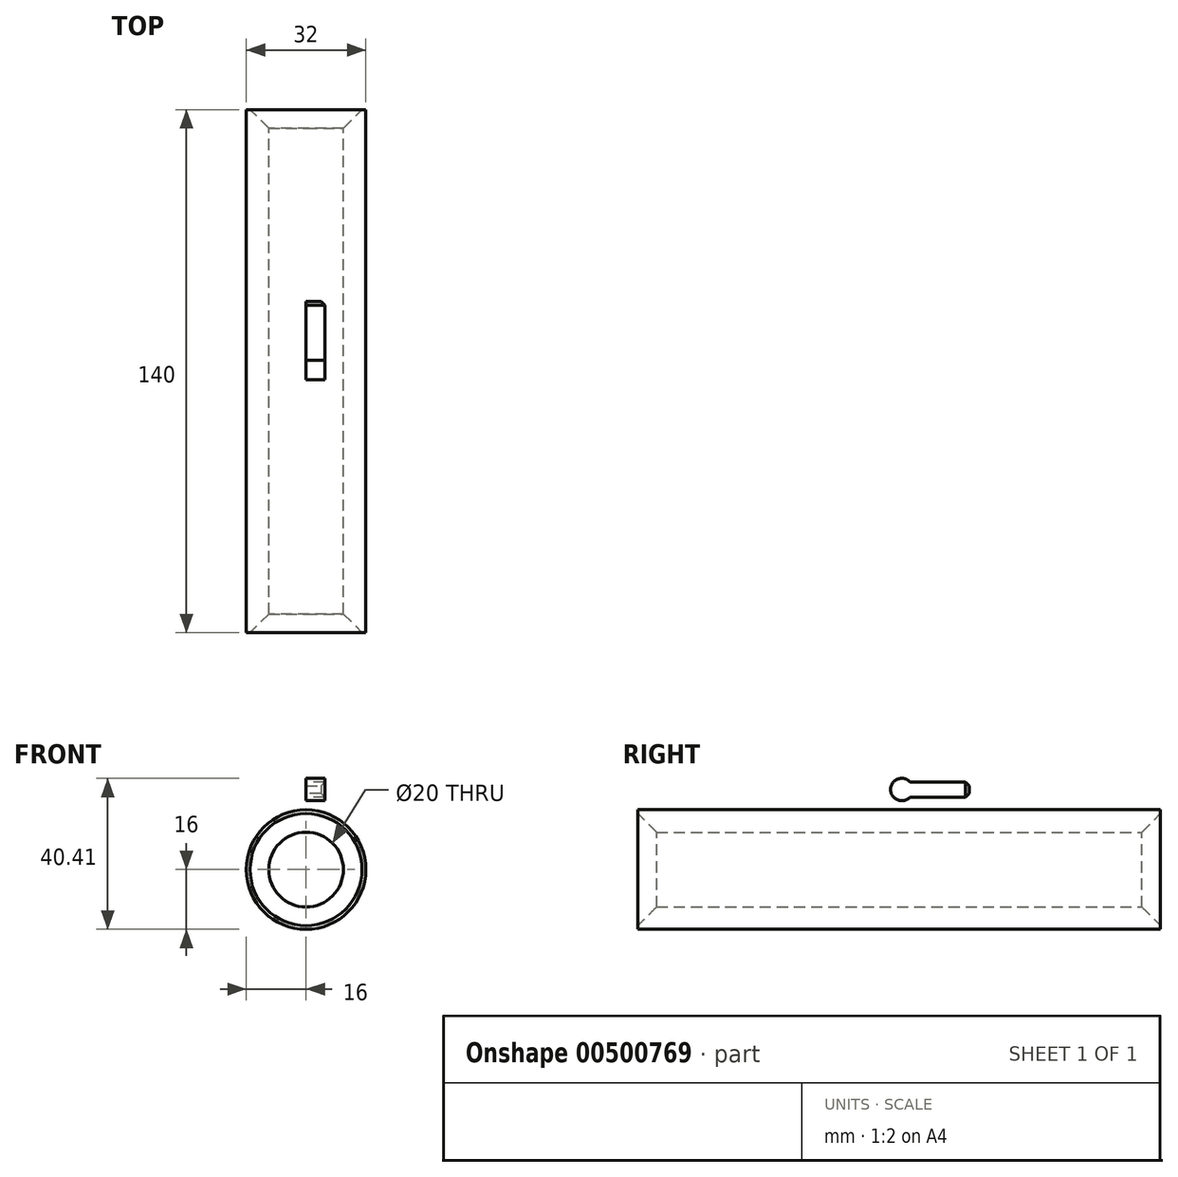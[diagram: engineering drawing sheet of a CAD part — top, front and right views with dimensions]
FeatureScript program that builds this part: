
annotation { "Feature Type Name" : "Feature", "Feature Type Description" : "" }
export const myFeature = defineFeature(function(context is Context, id is Id, definition is map)
    precondition{}
    {
        {
            var Q0;
            Q0=qCreatedBy(makeId("Front.planeOp"),FACE);
            var sketch = newSketch(context, id + "F0", { "sketchPlane" : qUnion([Q0])});
            skCircle(sketch, "E0", {"center": v(0, 0) * mm, "radius": 10 * mm});
            skCircle(sketch, "E1", {"center": v(0, 0) * mm, "radius": 16 * mm});
            skSolve(sketch);
        }
        {
            var Q0;
            Q0=makeQuery(id+"F0.imprint","IMPRINT",FACE,{"disambiguationData":[TD([[makeQuery(id+"F0.imprint","IMPRINT",EDGE,{"derivedFrom":sQuery(id+"F0.wireOp",EDGE,"E0")}),-1.0]])]});
            extrude(context, id + "F1", {"entities" : qUnion([Q0]), "depth" : 140 * mm});
        }
        {
            var Q0;
            Q0=makeQuery(id+"F1.opExtrude","CAP_EDGE",EDGE,{"disambiguationData":[OSD([sQuery(id+"F0.wireOp",EDGE,"E0")])],"isStart":false});
            var Q1;
            Q1=makeQuery(id+"F1.opExtrude","CAP_EDGE",EDGE,{"disambiguationData":[OSD([sQuery(id+"F0.wireOp",EDGE,"E0")])],"isStart":true});
            chamfer(context, id + "F2", {"entities" : qUnion([Q0, Q1]), "width" : 5 * mm, "tangentPropagation" : true});
        }
        {
            var Q0;
            Q0=qCreatedBy(makeId("Right.planeOp"),FACE);
            var sketch = newSketch(context, id + "F3", { "sketchPlane" : qUnion([Q0])});
            skLineSegment(sketch, "E2.bottom", {"start": v(-69.3, 23.4) * mm, "end": v(-51.3, 23.4) * mm});
            skLineSegment(sketch, "E2.top", {"start": v(-69.3, 19.4) * mm, "end": v(-51.3, 19.4) * mm});
            skLineSegment(sketch, "E2.left", {"start": v(-69.3, 23.4) * mm, "end": v(-69.3, 19.4) * mm});
            skLineSegment(sketch, "E2.right", {"start": v(-51.3, 23.4) * mm, "end": v(-51.3, 19.4) * mm});
            skCircle(sketch, "E3", {"center": v(-69.3, 21.4) * mm, "radius": 3 * mm});
            skSolve(sketch);
        }
        {
            var Q0;
            {var subQ0=sQuery(id+"F3.wireOp",EDGE,"E2.right");Q0=makeQuery(id+"F3.imprint","IMPRINT",FACE,{"disambiguationData":[TD([[makeQuery(id+"F3.imprint","IMPRINT",EDGE,{"derivedFrom":subQ0}),-1.0]])]});}
            var Q1;
            {var subQ0=sQuery(id+"F3.wireOp",EDGE,"E2.left");Q1=makeQuery(id+"F3.imprint","IMPRINT",FACE,{"disambiguationData":[TD([[makeQuery(id+"F3.imprint","IMPRINT",EDGE,{"derivedFrom":subQ0}),1.0]])]});}
            var Q2;
            {var subQ0=sQuery(id+"F3.wireOp",EDGE,"E2.left");Q2=makeQuery(id+"F3.imprint","IMPRINT",FACE,{"disambiguationData":[TD([[makeQuery(id+"F3.imprint","IMPRINT",EDGE,{"derivedFrom":subQ0}),-1.0]])]});}
            extrude(context, id + "F4", {"entities" : qUnion([Q0, Q1, Q2]), "depth" : 5 * mm});
        }
        {
            var Q0;
            Q0=makeQuery(id+"F4.opExtrude","SWEPT_EDGE",EDGE,{"disambiguationData":[OSD([sQuery(id+"F3.wireOp",EDGE,"E2.bottom"),sQuery(id+"F3.wireOp",EDGE,"E2.right")])]});
            var Q1;
            Q1=makeQuery(id+"F4.opExtrude","SWEPT_EDGE",EDGE,{"disambiguationData":[OSD([sQuery(id+"F3.wireOp",EDGE,"E2.top"),sQuery(id+"F3.wireOp",EDGE,"E2.right")])]});
            var Q2;
            Q2=makeQuery(id+"F4.opExtrude","CAP_EDGE",EDGE,{"disambiguationData":[OSD([sQuery(id+"F3.wireOp",EDGE,"E2.right")])],"isStart":false});
            chamfer(context, id + "F5", {"entities" : qUnion([Q0, Q1, Q2]), "width" : 1 * mm, "tangentPropagation" : true});
        }
    });
